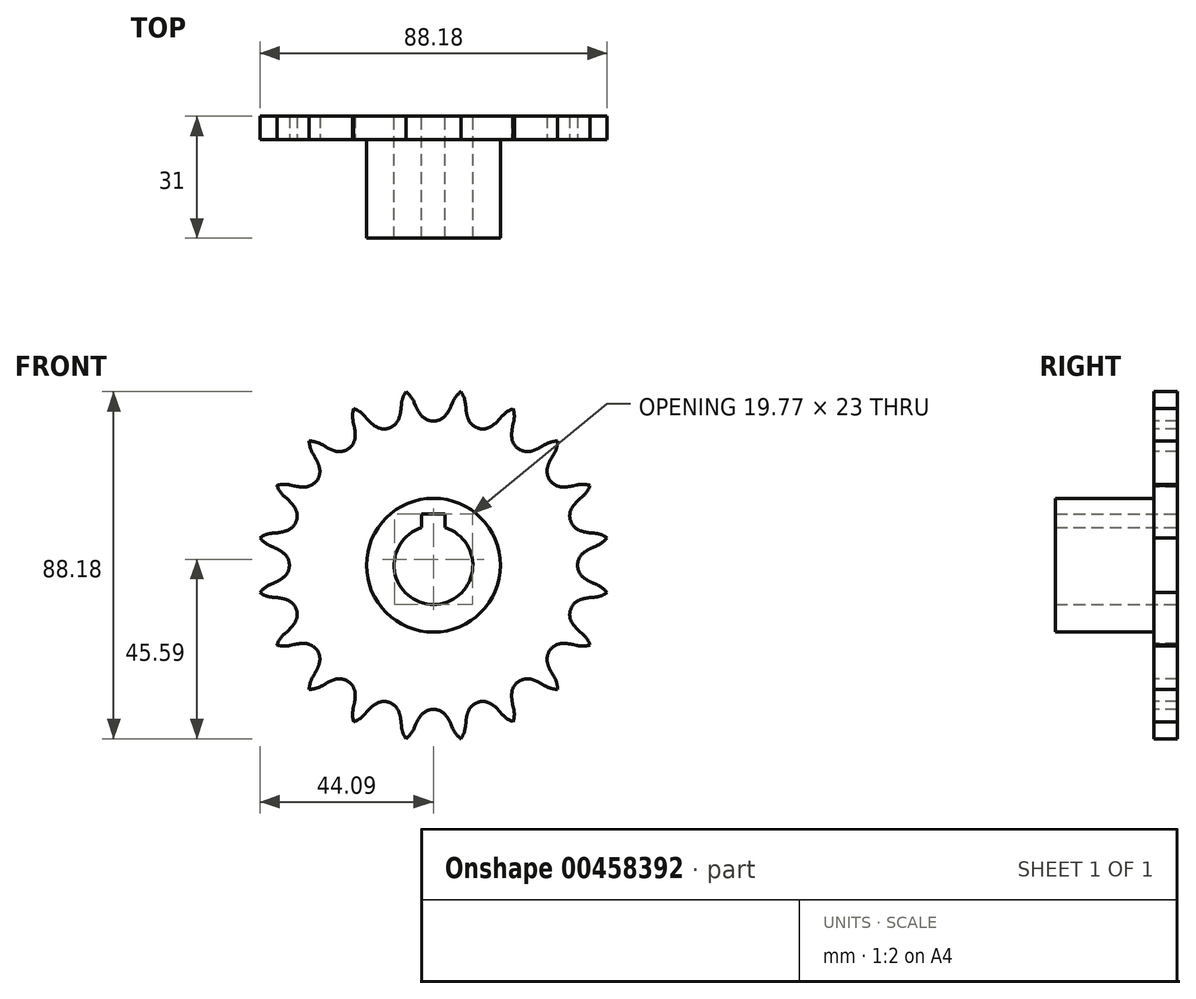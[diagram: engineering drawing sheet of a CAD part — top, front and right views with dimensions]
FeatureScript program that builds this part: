
annotation { "Feature Type Name" : "Feature", "Feature Type Description" : "" }
export const myFeature = defineFeature(function(context is Context, id is Id, definition is map)
    precondition{}
    {
        {
            var Q0;
            Q0=qCreatedBy(makeId("Front.planeOp"),FACE);
            var sketch = newSketch(context, id + "F0", { "sketchPlane" : qUnion([Q0])});
            skCircle(sketch, "E0", {"center": v(0, 0) * mm, "radius": 40.6 * mm, "construction": true});
            skLineSegment(sketch, "E1", {"start": v(0, 40.6) * mm, "end": v(5, 44.5) * mm, "construction": true});
            skLineSegment(sketch, "E2", {"start": v(-4.52, 40.5) * mm, "end": v(-4.9, 41.4) * mm});
            skLineSegment(sketch, "E3", {"start": v(0, 40.6) * mm, "end": v(17.06, 40.6) * mm, "construction": true});
            skArc(sketch, "E4", {"start": v(-4.52, 40.5) * mm, "mid": v(-3.9, 39.27) * mm, "end": v(-3.14, 38.14) * mm});
            skArc(sketch, "E5", {"start": v(-4.9, 41.4) * mm, "mid": v(-5.76, 42.88) * mm, "end": v(-6.98, 44.09) * mm});
            skLineSegment(sketch, "E6", {"start": v(0, 0) * mm, "end": v(-7.77, 49.08) * mm, "construction": true});
            skArc(sketch, "E7.trimOffspring", {"start": v(-3.14, 38.14) * mm, "mid": v(-1.75, 37.01) * mm, "end": v(0, 36.61) * mm});
            skArc(sketch, "E8.trimOffspring", {"start": v(13.29, 38.36) * mm, "mid": v(13.99, 39.43) * mm, "end": v(14.54, 40.6) * mm});
            skLineSegment(sketch, "E9", {"start": v(0, 40.6) * mm, "end": v(0, 0) * mm, "construction": true});
            skArc(sketch, "E10.MirrorCS", {"start": v(4.9, 41.4) * mm, "mid": v(5.76, 42.88) * mm, "end": v(6.98, 44.09) * mm});
            skLineSegment(sketch, "E11.MirrorCS", {"start": v(4.52, 40.5) * mm, "end": v(4.9, 41.4) * mm});
            skArc(sketch, "E12.MirrorCS", {"start": v(4.52, 40.5) * mm, "mid": v(3.9, 39.27) * mm, "end": v(3.14, 38.14) * mm});
            skArc(sketch, "E13.MirrorCS", {"start": v(3.14, 38.14) * mm, "mid": v(1.75, 37.01) * mm, "end": v(0, 36.61) * mm});
            skArc(sketch, "E14.1.0", {"start": v(-17.45, 37.86) * mm, "mid": v(-18.73, 39) * mm, "end": v(-20.26, 39.77) * mm});
            skArc(sketch, "E14.1.1", {"start": v(-16.81, 37.12) * mm, "mid": v(-15.85, 36.14) * mm, "end": v(-14.77, 35.3) * mm});
            skLineSegment(sketch, "E14.1.2", {"start": v(-16.81, 37.12) * mm, "end": v(-17.45, 37.86) * mm});
            skArc(sketch, "E14.1.3", {"start": v(-14.77, 35.3) * mm, "mid": v(-13.1, 34.66) * mm, "end": v(-11.31, 34.82) * mm});
            skArc(sketch, "E14.1.4", {"start": v(-8.8, 37.24) * mm, "mid": v(-9.78, 35.74) * mm, "end": v(-11.31, 34.82) * mm});
            skArc(sketch, "E14.1.5", {"start": v(-8.22, 39.9) * mm, "mid": v(-8.42, 38.56) * mm, "end": v(-8.8, 37.24) * mm});
            skLineSegment(sketch, "E14.1.6", {"start": v(-8.22, 39.9) * mm, "end": v(-8.13, 40.89) * mm});
            skArc(sketch, "E14.1.7", {"start": v(-8.13, 40.89) * mm, "mid": v(-7.77, 42.56) * mm, "end": v(-6.98, 44.09) * mm});
            skArc(sketch, "E14.2.0", {"start": v(-28.3, 30.61) * mm, "mid": v(-29.87, 31.3) * mm, "end": v(-31.56, 31.56) * mm});
            skArc(sketch, "E14.2.1", {"start": v(-27.46, 30.1) * mm, "mid": v(-26.24, 29.48) * mm, "end": v(-24.96, 29.01) * mm});
            skLineSegment(sketch, "E14.2.2", {"start": v(-27.46, 30.1) * mm, "end": v(-28.3, 30.61) * mm});
            skArc(sketch, "E14.2.3", {"start": v(-24.96, 29.01) * mm, "mid": v(-23.17, 28.92) * mm, "end": v(-21.52, 29.62) * mm});
            skArc(sketch, "E14.2.4", {"start": v(-19.88, 32.7) * mm, "mid": v(-20.34, 30.97) * mm, "end": v(-21.52, 29.62) * mm});
            skArc(sketch, "E14.2.5", {"start": v(-20.15, 35.42) * mm, "mid": v(-19.92, 34.07) * mm, "end": v(-19.88, 32.7) * mm});
            skLineSegment(sketch, "E14.2.6", {"start": v(-20.15, 35.42) * mm, "end": v(-20.37, 36.37) * mm});
            skArc(sketch, "E14.2.7", {"start": v(-20.37, 36.37) * mm, "mid": v(-20.54, 38.08) * mm, "end": v(-20.26, 39.77) * mm});
            skArc(sketch, "E14.3.0", {"start": v(-36.37, 20.37) * mm, "mid": v(-38.08, 20.54) * mm, "end": v(-39.77, 20.26) * mm});
            skArc(sketch, "E14.3.1", {"start": v(-35.42, 20.15) * mm, "mid": v(-34.07, 19.92) * mm, "end": v(-32.7, 19.88) * mm});
            skLineSegment(sketch, "E14.3.2", {"start": v(-35.42, 20.15) * mm, "end": v(-36.37, 20.37) * mm});
            skArc(sketch, "E14.3.3", {"start": v(-32.7, 19.88) * mm, "mid": v(-30.97, 20.34) * mm, "end": v(-29.62, 21.52) * mm});
            skArc(sketch, "E14.3.4", {"start": v(-29.01, 24.96) * mm, "mid": v(-28.92, 23.17) * mm, "end": v(-29.62, 21.52) * mm});
            skArc(sketch, "E14.3.5", {"start": v(-30.1, 27.46) * mm, "mid": v(-29.48, 26.24) * mm, "end": v(-29.01, 24.96) * mm});
            skLineSegment(sketch, "E14.3.6", {"start": v(-30.1, 27.46) * mm, "end": v(-30.61, 28.3) * mm});
            skArc(sketch, "E14.3.7", {"start": v(-30.61, 28.3) * mm, "mid": v(-31.3, 29.87) * mm, "end": v(-31.56, 31.56) * mm});
            skArc(sketch, "E14.4.0", {"start": v(-40.89, 8.13) * mm, "mid": v(-42.56, 7.77) * mm, "end": v(-44.09, 6.98) * mm});
            skArc(sketch, "E14.4.1", {"start": v(-39.9, 8.22) * mm, "mid": v(-38.56, 8.42) * mm, "end": v(-37.24, 8.8) * mm});
            skLineSegment(sketch, "E14.4.2", {"start": v(-39.9, 8.22) * mm, "end": v(-40.89, 8.13) * mm});
            skArc(sketch, "E14.4.3", {"start": v(-37.24, 8.8) * mm, "mid": v(-35.74, 9.78) * mm, "end": v(-34.82, 11.31) * mm});
            skArc(sketch, "E14.4.4", {"start": v(-35.3, 14.77) * mm, "mid": v(-34.66, 13.1) * mm, "end": v(-34.82, 11.31) * mm});
            skArc(sketch, "E14.4.5", {"start": v(-37.12, 16.81) * mm, "mid": v(-36.14, 15.85) * mm, "end": v(-35.3, 14.77) * mm});
            skLineSegment(sketch, "E14.4.6", {"start": v(-37.12, 16.81) * mm, "end": v(-37.86, 17.45) * mm});
            skArc(sketch, "E14.4.7", {"start": v(-37.86, 17.45) * mm, "mid": v(-39, 18.73) * mm, "end": v(-39.77, 20.26) * mm});
            skArc(sketch, "E14.5.0", {"start": v(-41.4, -4.9) * mm, "mid": v(-42.88, -5.76) * mm, "end": v(-44.09, -6.98) * mm});
            skArc(sketch, "E14.5.1", {"start": v(-40.5, -4.52) * mm, "mid": v(-39.27, -3.9) * mm, "end": v(-38.14, -3.14) * mm});
            skLineSegment(sketch, "E14.5.2", {"start": v(-40.5, -4.52) * mm, "end": v(-41.4, -4.9) * mm});
            skArc(sketch, "E14.5.3", {"start": v(-38.14, -3.14) * mm, "mid": v(-37.01, -1.75) * mm, "end": v(-36.61, 0) * mm});
            skArc(sketch, "E14.5.4", {"start": v(-38.14, 3.14) * mm, "mid": v(-37.01, 1.75) * mm, "end": v(-36.61, 0) * mm});
            skArc(sketch, "E14.5.5", {"start": v(-40.5, 4.52) * mm, "mid": v(-39.27, 3.9) * mm, "end": v(-38.14, 3.14) * mm});
            skLineSegment(sketch, "E14.5.6", {"start": v(-40.5, 4.52) * mm, "end": v(-41.4, 4.9) * mm});
            skArc(sketch, "E14.5.7", {"start": v(-41.4, 4.9) * mm, "mid": v(-42.88, 5.76) * mm, "end": v(-44.09, 6.98) * mm});
            skArc(sketch, "E14.6.0", {"start": v(-37.86, -17.45) * mm, "mid": v(-39, -18.73) * mm, "end": v(-39.77, -20.26) * mm});
            skArc(sketch, "E14.6.1", {"start": v(-37.12, -16.81) * mm, "mid": v(-36.14, -15.85) * mm, "end": v(-35.3, -14.77) * mm});
            skLineSegment(sketch, "E14.6.2", {"start": v(-37.12, -16.81) * mm, "end": v(-37.86, -17.45) * mm});
            skArc(sketch, "E14.6.3", {"start": v(-35.3, -14.77) * mm, "mid": v(-34.66, -13.1) * mm, "end": v(-34.82, -11.31) * mm});
            skArc(sketch, "E14.6.4", {"start": v(-37.24, -8.8) * mm, "mid": v(-35.74, -9.78) * mm, "end": v(-34.82, -11.31) * mm});
            skArc(sketch, "E14.6.5", {"start": v(-39.9, -8.22) * mm, "mid": v(-38.56, -8.42) * mm, "end": v(-37.24, -8.8) * mm});
            skLineSegment(sketch, "E14.6.6", {"start": v(-39.9, -8.22) * mm, "end": v(-40.89, -8.13) * mm});
            skArc(sketch, "E14.6.7", {"start": v(-40.89, -8.13) * mm, "mid": v(-42.56, -7.77) * mm, "end": v(-44.09, -6.98) * mm});
            skArc(sketch, "E14.7.0", {"start": v(-30.61, -28.3) * mm, "mid": v(-31.3, -29.87) * mm, "end": v(-31.56, -31.56) * mm});
            skArc(sketch, "E14.7.1", {"start": v(-30.1, -27.46) * mm, "mid": v(-29.48, -26.24) * mm, "end": v(-29.01, -24.96) * mm});
            skLineSegment(sketch, "E14.7.2", {"start": v(-30.1, -27.46) * mm, "end": v(-30.61, -28.3) * mm});
            skArc(sketch, "E14.7.3", {"start": v(-29.01, -24.96) * mm, "mid": v(-28.92, -23.17) * mm, "end": v(-29.62, -21.52) * mm});
            skArc(sketch, "E14.7.4", {"start": v(-32.7, -19.88) * mm, "mid": v(-30.97, -20.34) * mm, "end": v(-29.62, -21.52) * mm});
            skArc(sketch, "E14.7.5", {"start": v(-35.42, -20.15) * mm, "mid": v(-34.07, -19.92) * mm, "end": v(-32.7, -19.88) * mm});
            skLineSegment(sketch, "E14.7.6", {"start": v(-35.42, -20.15) * mm, "end": v(-36.37, -20.37) * mm});
            skArc(sketch, "E14.7.7", {"start": v(-36.37, -20.37) * mm, "mid": v(-38.08, -20.54) * mm, "end": v(-39.77, -20.26) * mm});
            skArc(sketch, "E14.8.0", {"start": v(-20.37, -36.37) * mm, "mid": v(-20.54, -38.08) * mm, "end": v(-20.26, -39.77) * mm});
            skArc(sketch, "E14.8.1", {"start": v(-20.15, -35.42) * mm, "mid": v(-19.92, -34.07) * mm, "end": v(-19.88, -32.7) * mm});
            skLineSegment(sketch, "E14.8.2", {"start": v(-20.15, -35.42) * mm, "end": v(-20.37, -36.37) * mm});
            skArc(sketch, "E14.8.3", {"start": v(-19.88, -32.7) * mm, "mid": v(-20.34, -30.97) * mm, "end": v(-21.52, -29.62) * mm});
            skArc(sketch, "E14.8.4", {"start": v(-24.96, -29.01) * mm, "mid": v(-23.17, -28.92) * mm, "end": v(-21.52, -29.62) * mm});
            skArc(sketch, "E14.8.5", {"start": v(-27.46, -30.1) * mm, "mid": v(-26.24, -29.48) * mm, "end": v(-24.96, -29.01) * mm});
            skLineSegment(sketch, "E14.8.6", {"start": v(-27.46, -30.1) * mm, "end": v(-28.3, -30.61) * mm});
            skArc(sketch, "E14.8.7", {"start": v(-28.3, -30.61) * mm, "mid": v(-29.87, -31.3) * mm, "end": v(-31.56, -31.56) * mm});
            skArc(sketch, "E14.9.0", {"start": v(-8.13, -40.89) * mm, "mid": v(-7.77, -42.56) * mm, "end": v(-6.98, -44.09) * mm});
            skArc(sketch, "E14.9.1", {"start": v(-8.22, -39.9) * mm, "mid": v(-8.42, -38.56) * mm, "end": v(-8.8, -37.24) * mm});
            skLineSegment(sketch, "E14.9.2", {"start": v(-8.22, -39.9) * mm, "end": v(-8.13, -40.89) * mm});
            skArc(sketch, "E14.9.3", {"start": v(-8.8, -37.24) * mm, "mid": v(-9.78, -35.74) * mm, "end": v(-11.31, -34.82) * mm});
            skArc(sketch, "E14.9.4", {"start": v(-14.77, -35.3) * mm, "mid": v(-13.1, -34.66) * mm, "end": v(-11.31, -34.82) * mm});
            skArc(sketch, "E14.9.5", {"start": v(-16.81, -37.12) * mm, "mid": v(-15.85, -36.14) * mm, "end": v(-14.77, -35.3) * mm});
            skLineSegment(sketch, "E14.9.6", {"start": v(-16.81, -37.12) * mm, "end": v(-17.45, -37.86) * mm});
            skArc(sketch, "E14.9.7", {"start": v(-17.45, -37.86) * mm, "mid": v(-18.73, -39) * mm, "end": v(-20.26, -39.77) * mm});
            skArc(sketch, "E14.10.0", {"start": v(4.9, -41.4) * mm, "mid": v(5.76, -42.88) * mm, "end": v(6.98, -44.09) * mm});
            skArc(sketch, "E14.10.1", {"start": v(4.52, -40.5) * mm, "mid": v(3.9, -39.27) * mm, "end": v(3.14, -38.14) * mm});
            skLineSegment(sketch, "E14.10.2", {"start": v(4.52, -40.5) * mm, "end": v(4.9, -41.4) * mm});
            skArc(sketch, "E14.10.3", {"start": v(3.14, -38.14) * mm, "mid": v(1.75, -37.01) * mm, "end": v(0, -36.61) * mm});
            skArc(sketch, "E14.10.4", {"start": v(-3.14, -38.14) * mm, "mid": v(-1.75, -37.01) * mm, "end": v(0, -36.61) * mm});
            skArc(sketch, "E14.10.5", {"start": v(-4.52, -40.5) * mm, "mid": v(-3.9, -39.27) * mm, "end": v(-3.14, -38.14) * mm});
            skLineSegment(sketch, "E14.10.6", {"start": v(-4.52, -40.5) * mm, "end": v(-4.9, -41.4) * mm});
            skArc(sketch, "E14.10.7", {"start": v(-4.9, -41.4) * mm, "mid": v(-5.76, -42.88) * mm, "end": v(-6.98, -44.09) * mm});
            skArc(sketch, "E14.11.0", {"start": v(17.45, -37.86) * mm, "mid": v(18.73, -39) * mm, "end": v(20.26, -39.77) * mm});
            skArc(sketch, "E14.11.1", {"start": v(16.81, -37.12) * mm, "mid": v(15.85, -36.14) * mm, "end": v(14.77, -35.3) * mm});
            skLineSegment(sketch, "E14.11.2", {"start": v(16.81, -37.12) * mm, "end": v(17.45, -37.86) * mm});
            skArc(sketch, "E14.11.3", {"start": v(14.77, -35.3) * mm, "mid": v(13.1, -34.66) * mm, "end": v(11.31, -34.82) * mm});
            skArc(sketch, "E14.11.4", {"start": v(8.8, -37.24) * mm, "mid": v(9.78, -35.74) * mm, "end": v(11.31, -34.82) * mm});
            skArc(sketch, "E14.11.5", {"start": v(8.22, -39.9) * mm, "mid": v(8.42, -38.56) * mm, "end": v(8.8, -37.24) * mm});
            skLineSegment(sketch, "E14.11.6", {"start": v(8.22, -39.9) * mm, "end": v(8.13, -40.89) * mm});
            skArc(sketch, "E14.11.7", {"start": v(8.13, -40.89) * mm, "mid": v(7.77, -42.56) * mm, "end": v(6.98, -44.09) * mm});
            skArc(sketch, "E14.12.0", {"start": v(28.3, -30.61) * mm, "mid": v(29.87, -31.3) * mm, "end": v(31.56, -31.56) * mm});
            skArc(sketch, "E14.12.1", {"start": v(27.46, -30.1) * mm, "mid": v(26.24, -29.48) * mm, "end": v(24.96, -29.01) * mm});
            skLineSegment(sketch, "E14.12.2", {"start": v(27.46, -30.1) * mm, "end": v(28.3, -30.61) * mm});
            skArc(sketch, "E14.12.3", {"start": v(24.96, -29.01) * mm, "mid": v(23.17, -28.92) * mm, "end": v(21.52, -29.62) * mm});
            skArc(sketch, "E14.12.4", {"start": v(19.88, -32.7) * mm, "mid": v(20.34, -30.97) * mm, "end": v(21.52, -29.62) * mm});
            skArc(sketch, "E14.12.5", {"start": v(20.15, -35.42) * mm, "mid": v(19.92, -34.07) * mm, "end": v(19.88, -32.7) * mm});
            skLineSegment(sketch, "E14.12.6", {"start": v(20.15, -35.42) * mm, "end": v(20.37, -36.37) * mm});
            skArc(sketch, "E14.12.7", {"start": v(20.37, -36.37) * mm, "mid": v(20.54, -38.08) * mm, "end": v(20.26, -39.77) * mm});
            skArc(sketch, "E14.13.0", {"start": v(36.37, -20.37) * mm, "mid": v(38.08, -20.54) * mm, "end": v(39.77, -20.26) * mm});
            skArc(sketch, "E14.13.1", {"start": v(35.42, -20.15) * mm, "mid": v(34.07, -19.92) * mm, "end": v(32.7, -19.88) * mm});
            skLineSegment(sketch, "E14.13.2", {"start": v(35.42, -20.15) * mm, "end": v(36.37, -20.37) * mm});
            skArc(sketch, "E14.13.3", {"start": v(32.7, -19.88) * mm, "mid": v(30.97, -20.34) * mm, "end": v(29.62, -21.52) * mm});
            skArc(sketch, "E14.13.4", {"start": v(29.01, -24.96) * mm, "mid": v(28.92, -23.17) * mm, "end": v(29.62, -21.52) * mm});
            skArc(sketch, "E14.13.5", {"start": v(30.1, -27.46) * mm, "mid": v(29.48, -26.24) * mm, "end": v(29.01, -24.96) * mm});
            skLineSegment(sketch, "E14.13.6", {"start": v(30.1, -27.46) * mm, "end": v(30.61, -28.3) * mm});
            skArc(sketch, "E14.13.7", {"start": v(30.61, -28.3) * mm, "mid": v(31.3, -29.87) * mm, "end": v(31.56, -31.56) * mm});
            skArc(sketch, "E14.14.0", {"start": v(40.89, -8.13) * mm, "mid": v(42.56, -7.77) * mm, "end": v(44.09, -6.98) * mm});
            skArc(sketch, "E14.14.1", {"start": v(39.9, -8.22) * mm, "mid": v(38.56, -8.42) * mm, "end": v(37.24, -8.8) * mm});
            skLineSegment(sketch, "E14.14.2", {"start": v(39.9, -8.22) * mm, "end": v(40.89, -8.13) * mm});
            skArc(sketch, "E14.14.3", {"start": v(37.24, -8.8) * mm, "mid": v(35.74, -9.78) * mm, "end": v(34.82, -11.31) * mm});
            skArc(sketch, "E14.14.4", {"start": v(35.3, -14.77) * mm, "mid": v(34.66, -13.1) * mm, "end": v(34.82, -11.31) * mm});
            skArc(sketch, "E14.14.5", {"start": v(37.12, -16.81) * mm, "mid": v(36.14, -15.85) * mm, "end": v(35.3, -14.77) * mm});
            skLineSegment(sketch, "E14.14.6", {"start": v(37.12, -16.81) * mm, "end": v(37.86, -17.45) * mm});
            skArc(sketch, "E14.14.7", {"start": v(37.86, -17.45) * mm, "mid": v(39, -18.73) * mm, "end": v(39.77, -20.26) * mm});
            skArc(sketch, "E14.15.0", {"start": v(41.4, 4.9) * mm, "mid": v(42.88, 5.76) * mm, "end": v(44.09, 6.98) * mm});
            skArc(sketch, "E14.15.1", {"start": v(40.5, 4.52) * mm, "mid": v(39.27, 3.9) * mm, "end": v(38.14, 3.14) * mm});
            skLineSegment(sketch, "E14.15.2", {"start": v(40.5, 4.52) * mm, "end": v(41.4, 4.9) * mm});
            skArc(sketch, "E14.15.3", {"start": v(38.14, 3.14) * mm, "mid": v(37.01, 1.75) * mm, "end": v(36.61, 0) * mm});
            skArc(sketch, "E14.15.4", {"start": v(38.14, -3.14) * mm, "mid": v(37.01, -1.75) * mm, "end": v(36.61, 0) * mm});
            skArc(sketch, "E14.15.5", {"start": v(40.5, -4.52) * mm, "mid": v(39.27, -3.9) * mm, "end": v(38.14, -3.14) * mm});
            skLineSegment(sketch, "E14.15.6", {"start": v(40.5, -4.52) * mm, "end": v(41.4, -4.9) * mm});
            skArc(sketch, "E14.15.7", {"start": v(41.4, -4.9) * mm, "mid": v(42.88, -5.76) * mm, "end": v(44.09, -6.98) * mm});
            skArc(sketch, "E14.16.0", {"start": v(37.86, 17.45) * mm, "mid": v(39, 18.73) * mm, "end": v(39.77, 20.26) * mm});
            skArc(sketch, "E14.16.1", {"start": v(37.12, 16.81) * mm, "mid": v(36.14, 15.85) * mm, "end": v(35.3, 14.77) * mm});
            skLineSegment(sketch, "E14.16.2", {"start": v(37.12, 16.81) * mm, "end": v(37.86, 17.45) * mm});
            skArc(sketch, "E14.16.3", {"start": v(35.3, 14.77) * mm, "mid": v(34.66, 13.1) * mm, "end": v(34.82, 11.31) * mm});
            skArc(sketch, "E14.16.4", {"start": v(37.24, 8.8) * mm, "mid": v(35.74, 9.78) * mm, "end": v(34.82, 11.31) * mm});
            skArc(sketch, "E14.16.5", {"start": v(39.9, 8.22) * mm, "mid": v(38.56, 8.42) * mm, "end": v(37.24, 8.8) * mm});
            skLineSegment(sketch, "E14.16.6", {"start": v(39.9, 8.22) * mm, "end": v(40.89, 8.13) * mm});
            skArc(sketch, "E14.16.7", {"start": v(40.89, 8.13) * mm, "mid": v(42.56, 7.77) * mm, "end": v(44.09, 6.98) * mm});
            skArc(sketch, "E14.17.0", {"start": v(30.61, 28.3) * mm, "mid": v(31.3, 29.87) * mm, "end": v(31.56, 31.56) * mm});
            skArc(sketch, "E14.17.1", {"start": v(30.1, 27.46) * mm, "mid": v(29.48, 26.24) * mm, "end": v(29.01, 24.96) * mm});
            skLineSegment(sketch, "E14.17.2", {"start": v(30.1, 27.46) * mm, "end": v(30.61, 28.3) * mm});
            skArc(sketch, "E14.17.3", {"start": v(29.01, 24.96) * mm, "mid": v(28.92, 23.17) * mm, "end": v(29.62, 21.52) * mm});
            skArc(sketch, "E14.17.4", {"start": v(32.7, 19.88) * mm, "mid": v(30.97, 20.34) * mm, "end": v(29.62, 21.52) * mm});
            skArc(sketch, "E14.17.5", {"start": v(35.42, 20.15) * mm, "mid": v(34.07, 19.92) * mm, "end": v(32.7, 19.88) * mm});
            skLineSegment(sketch, "E14.17.6", {"start": v(35.42, 20.15) * mm, "end": v(36.37, 20.37) * mm});
            skArc(sketch, "E14.17.7", {"start": v(36.37, 20.37) * mm, "mid": v(38.08, 20.54) * mm, "end": v(39.77, 20.26) * mm});
            skArc(sketch, "E14.18.0", {"start": v(20.37, 36.37) * mm, "mid": v(20.54, 38.08) * mm, "end": v(20.26, 39.77) * mm});
            skArc(sketch, "E14.18.1", {"start": v(20.15, 35.42) * mm, "mid": v(19.92, 34.07) * mm, "end": v(19.88, 32.7) * mm});
            skLineSegment(sketch, "E14.18.2", {"start": v(20.15, 35.42) * mm, "end": v(20.37, 36.37) * mm});
            skArc(sketch, "E14.18.3", {"start": v(19.88, 32.7) * mm, "mid": v(20.34, 30.97) * mm, "end": v(21.52, 29.62) * mm});
            skArc(sketch, "E14.18.4", {"start": v(24.96, 29.01) * mm, "mid": v(23.17, 28.92) * mm, "end": v(21.52, 29.62) * mm});
            skArc(sketch, "E14.18.5", {"start": v(27.46, 30.1) * mm, "mid": v(26.24, 29.48) * mm, "end": v(24.96, 29.01) * mm});
            skLineSegment(sketch, "E14.18.6", {"start": v(27.46, 30.1) * mm, "end": v(28.3, 30.61) * mm});
            skArc(sketch, "E14.18.7", {"start": v(28.3, 30.61) * mm, "mid": v(29.87, 31.3) * mm, "end": v(31.56, 31.56) * mm});
            skArc(sketch, "E14.19.0", {"start": v(8.13, 40.89) * mm, "mid": v(7.77, 42.56) * mm, "end": v(6.98, 44.09) * mm});
            skArc(sketch, "E14.19.1", {"start": v(8.22, 39.9) * mm, "mid": v(8.42, 38.56) * mm, "end": v(8.8, 37.24) * mm});
            skLineSegment(sketch, "E14.19.2", {"start": v(8.22, 39.9) * mm, "end": v(8.13, 40.89) * mm});
            skArc(sketch, "E14.19.3", {"start": v(8.8, 37.24) * mm, "mid": v(9.78, 35.74) * mm, "end": v(11.31, 34.82) * mm});
            skArc(sketch, "E14.19.4", {"start": v(14.77, 35.3) * mm, "mid": v(13.1, 34.66) * mm, "end": v(11.31, 34.82) * mm});
            skArc(sketch, "E14.19.5", {"start": v(16.81, 37.12) * mm, "mid": v(15.85, 36.14) * mm, "end": v(14.77, 35.3) * mm});
            skLineSegment(sketch, "E14.19.6", {"start": v(16.81, 37.12) * mm, "end": v(17.45, 37.86) * mm});
            skArc(sketch, "E14.19.7", {"start": v(17.45, 37.86) * mm, "mid": v(18.73, 39) * mm, "end": v(20.26, 39.77) * mm});
            skSolve(sketch);
        }
        {
            var Q0;
            Q0=makeQuery(id+"F0.imprint","IMPRINT",FACE,{"disambiguationData":[TD([[makeQuery(id+"F0.imprint","IMPRINT",EDGE,{"derivedFrom":sQuery(id+"F0.wireOp",EDGE,"E2")}),1.0]])]});
            extrude(context, id + "F1", {"entities" : qUnion([Q0]), "oppositeDirection" : true, "depth" : 6 * mm});
        }
        {
            var Q0;
            Q0=qCreatedBy(makeId("Front.planeOp"),FACE);
            var sketch = newSketch(context, id + "F2", { "sketchPlane" : qUnion([Q0])});
            skCircle(sketch, "E15", {"center": v(0, 0) * mm, "radius": 17 * mm});
            skCircle(sketch, "E16", {"center": v(0, 0) * mm, "radius": 10 * mm});
            skLineSegment(sketch, "E17.bottom", {"start": v(-3, 13) * mm, "end": v(3, 13) * mm});
            skLineSegment(sketch, "E17.top", {"start": v(-3, 7) * mm, "end": v(3, 7) * mm});
            skLineSegment(sketch, "E17.left", {"start": v(-3, 13) * mm, "end": v(-3, 7) * mm});
            skLineSegment(sketch, "E17.right", {"start": v(3, 13) * mm, "end": v(3, 7) * mm});
            skSolve(sketch);
        }
        {
            var Q0;
            Q0=makeQuery(id+"F2.imprint","IMPRINT",FACE,{"disambiguationData":[TD([[makeQuery(id+"F2.imprint","IMPRINT",EDGE,{"derivedFrom":sQuery(id+"F2.wireOp",EDGE,"E15")}),1.0]])]});
            extrude(context, id + "F3", {"entities" : qUnion([Q0]), "operationType" : NewBodyOperationType.ADD, "depth" : 25 * mm, "offsetDistance" : 25 * mm});
        }
        {
            var Q0;
            Q0=makeQuery(id+"F3.boolean.opBoolean","SPLIT",FACE,{"disambiguationData":[TD([makeQuery(id+"F3.opExtrude","SWEPT_FACE",FACE,{"disambiguationData":[OSD([sQuery(id+"F2.wireOp",EDGE,"E16")])]})])],"derivedFrom":makeQuery(id+"F1.opExtrude","CAP_FACE",FACE,{"disambiguationData":[OSD([sQuery(id+"F0.wireOp",EDGE,"E2"),sQuery(id+"F0.wireOp",EDGE,"E4"),sQuery(id+"F0.wireOp",EDGE,"E5"),sQuery(id+"F0.wireOp",EDGE,"E7.trimOffspring"),sQuery(id+"F0.wireOp",EDGE,"E10.MirrorCS"),sQuery(id+"F0.wireOp",EDGE,"E11.MirrorCS"),sQuery(id+"F0.wireOp",EDGE,"E12.MirrorCS"),sQuery(id+"F0.wireOp",EDGE,"E13.MirrorCS"),sQuery(id+"F0.wireOp",EDGE,"E14.1.0"),sQuery(id+"F0.wireOp",EDGE,"E14.1.1"),sQuery(id+"F0.wireOp",EDGE,"E14.1.2"),sQuery(id+"F0.wireOp",EDGE,"E14.1.3"),sQuery(id+"F0.wireOp",EDGE,"E14.1.4"),sQuery(id+"F0.wireOp",EDGE,"E14.1.5"),sQuery(id+"F0.wireOp",EDGE,"E14.1.6"),sQuery(id+"F0.wireOp",EDGE,"E14.1.7"),sQuery(id+"F0.wireOp",EDGE,"E14.2.0"),sQuery(id+"F0.wireOp",EDGE,"E14.2.1"),sQuery(id+"F0.wireOp",EDGE,"E14.2.2"),sQuery(id+"F0.wireOp",EDGE,"E14.2.3"),sQuery(id+"F0.wireOp",EDGE,"E14.2.4"),sQuery(id+"F0.wireOp",EDGE,"E14.2.5"),sQuery(id+"F0.wireOp",EDGE,"E14.2.6"),sQuery(id+"F0.wireOp",EDGE,"E14.2.7"),sQuery(id+"F0.wireOp",EDGE,"E14.3.0"),sQuery(id+"F0.wireOp",EDGE,"E14.3.1"),sQuery(id+"F0.wireOp",EDGE,"E14.3.2"),sQuery(id+"F0.wireOp",EDGE,"E14.3.3"),sQuery(id+"F0.wireOp",EDGE,"E14.3.4"),sQuery(id+"F0.wireOp",EDGE,"E14.3.5"),sQuery(id+"F0.wireOp",EDGE,"E14.3.6"),sQuery(id+"F0.wireOp",EDGE,"E14.3.7"),sQuery(id+"F0.wireOp",EDGE,"E14.4.0"),sQuery(id+"F0.wireOp",EDGE,"E14.4.1"),sQuery(id+"F0.wireOp",EDGE,"E14.4.2"),sQuery(id+"F0.wireOp",EDGE,"E14.4.3"),sQuery(id+"F0.wireOp",EDGE,"E14.4.4"),sQuery(id+"F0.wireOp",EDGE,"E14.4.5"),sQuery(id+"F0.wireOp",EDGE,"E14.4.6"),sQuery(id+"F0.wireOp",EDGE,"E14.4.7"),sQuery(id+"F0.wireOp",EDGE,"E14.5.0"),sQuery(id+"F0.wireOp",EDGE,"E14.5.1"),sQuery(id+"F0.wireOp",EDGE,"E14.5.2"),sQuery(id+"F0.wireOp",EDGE,"E14.5.3"),sQuery(id+"F0.wireOp",EDGE,"E14.5.4"),sQuery(id+"F0.wireOp",EDGE,"E14.5.5"),sQuery(id+"F0.wireOp",EDGE,"E14.5.6"),sQuery(id+"F0.wireOp",EDGE,"E14.5.7"),sQuery(id+"F0.wireOp",EDGE,"E14.6.0"),sQuery(id+"F0.wireOp",EDGE,"E14.6.1"),sQuery(id+"F0.wireOp",EDGE,"E14.6.2"),sQuery(id+"F0.wireOp",EDGE,"E14.6.3"),sQuery(id+"F0.wireOp",EDGE,"E14.6.4"),sQuery(id+"F0.wireOp",EDGE,"E14.6.5"),sQuery(id+"F0.wireOp",EDGE,"E14.6.6"),sQuery(id+"F0.wireOp",EDGE,"E14.6.7"),sQuery(id+"F0.wireOp",EDGE,"E14.7.0"),sQuery(id+"F0.wireOp",EDGE,"E14.7.1"),sQuery(id+"F0.wireOp",EDGE,"E14.7.2"),sQuery(id+"F0.wireOp",EDGE,"E14.7.3"),sQuery(id+"F0.wireOp",EDGE,"E14.7.4"),sQuery(id+"F0.wireOp",EDGE,"E14.7.5"),sQuery(id+"F0.wireOp",EDGE,"E14.7.6"),sQuery(id+"F0.wireOp",EDGE,"E14.7.7"),sQuery(id+"F0.wireOp",EDGE,"E14.8.0"),sQuery(id+"F0.wireOp",EDGE,"E14.8.1"),sQuery(id+"F0.wireOp",EDGE,"E14.8.2"),sQuery(id+"F0.wireOp",EDGE,"E14.8.3"),sQuery(id+"F0.wireOp",EDGE,"E14.8.4"),sQuery(id+"F0.wireOp",EDGE,"E14.8.5"),sQuery(id+"F0.wireOp",EDGE,"E14.8.6"),sQuery(id+"F0.wireOp",EDGE,"E14.8.7"),sQuery(id+"F0.wireOp",EDGE,"E14.9.0"),sQuery(id+"F0.wireOp",EDGE,"E14.9.1"),sQuery(id+"F0.wireOp",EDGE,"E14.9.2"),sQuery(id+"F0.wireOp",EDGE,"E14.9.3"),sQuery(id+"F0.wireOp",EDGE,"E14.9.4"),sQuery(id+"F0.wireOp",EDGE,"E14.9.5"),sQuery(id+"F0.wireOp",EDGE,"E14.9.6"),sQuery(id+"F0.wireOp",EDGE,"E14.9.7"),sQuery(id+"F0.wireOp",EDGE,"E14.10.0"),sQuery(id+"F0.wireOp",EDGE,"E14.10.1"),sQuery(id+"F0.wireOp",EDGE,"E14.10.2"),sQuery(id+"F0.wireOp",EDGE,"E14.10.3"),sQuery(id+"F0.wireOp",EDGE,"E14.10.4"),sQuery(id+"F0.wireOp",EDGE,"E14.10.5"),sQuery(id+"F0.wireOp",EDGE,"E14.10.6"),sQuery(id+"F0.wireOp",EDGE,"E14.10.7"),sQuery(id+"F0.wireOp",EDGE,"E14.11.0"),sQuery(id+"F0.wireOp",EDGE,"E14.11.1"),sQuery(id+"F0.wireOp",EDGE,"E14.11.2"),sQuery(id+"F0.wireOp",EDGE,"E14.11.3"),sQuery(id+"F0.wireOp",EDGE,"E14.11.4"),sQuery(id+"F0.wireOp",EDGE,"E14.11.5"),sQuery(id+"F0.wireOp",EDGE,"E14.11.6"),sQuery(id+"F0.wireOp",EDGE,"E14.11.7"),sQuery(id+"F0.wireOp",EDGE,"E14.12.0"),sQuery(id+"F0.wireOp",EDGE,"E14.12.1"),sQuery(id+"F0.wireOp",EDGE,"E14.12.2"),sQuery(id+"F0.wireOp",EDGE,"E14.12.3"),sQuery(id+"F0.wireOp",EDGE,"E14.12.4"),sQuery(id+"F0.wireOp",EDGE,"E14.12.5"),sQuery(id+"F0.wireOp",EDGE,"E14.12.6"),sQuery(id+"F0.wireOp",EDGE,"E14.12.7"),sQuery(id+"F0.wireOp",EDGE,"E14.13.0"),sQuery(id+"F0.wireOp",EDGE,"E14.13.1"),sQuery(id+"F0.wireOp",EDGE,"E14.13.2"),sQuery(id+"F0.wireOp",EDGE,"E14.13.3"),sQuery(id+"F0.wireOp",EDGE,"E14.13.4"),sQuery(id+"F0.wireOp",EDGE,"E14.13.5"),sQuery(id+"F0.wireOp",EDGE,"E14.13.6"),sQuery(id+"F0.wireOp",EDGE,"E14.13.7"),sQuery(id+"F0.wireOp",EDGE,"E14.14.0"),sQuery(id+"F0.wireOp",EDGE,"E14.14.1"),sQuery(id+"F0.wireOp",EDGE,"E14.14.2"),sQuery(id+"F0.wireOp",EDGE,"E14.14.3"),sQuery(id+"F0.wireOp",EDGE,"E14.14.4"),sQuery(id+"F0.wireOp",EDGE,"E14.14.5"),sQuery(id+"F0.wireOp",EDGE,"E14.14.6"),sQuery(id+"F0.wireOp",EDGE,"E14.14.7"),sQuery(id+"F0.wireOp",EDGE,"E14.15.0"),sQuery(id+"F0.wireOp",EDGE,"E14.15.1"),sQuery(id+"F0.wireOp",EDGE,"E14.15.2"),sQuery(id+"F0.wireOp",EDGE,"E14.15.3"),sQuery(id+"F0.wireOp",EDGE,"E14.15.4"),sQuery(id+"F0.wireOp",EDGE,"E14.15.5"),sQuery(id+"F0.wireOp",EDGE,"E14.15.6"),sQuery(id+"F0.wireOp",EDGE,"E14.15.7"),sQuery(id+"F0.wireOp",EDGE,"E14.16.0"),sQuery(id+"F0.wireOp",EDGE,"E14.16.1"),sQuery(id+"F0.wireOp",EDGE,"E14.16.2"),sQuery(id+"F0.wireOp",EDGE,"E14.16.3"),sQuery(id+"F0.wireOp",EDGE,"E14.16.4"),sQuery(id+"F0.wireOp",EDGE,"E14.16.5"),sQuery(id+"F0.wireOp",EDGE,"E14.16.6"),sQuery(id+"F0.wireOp",EDGE,"E14.16.7"),sQuery(id+"F0.wireOp",EDGE,"E14.17.0"),sQuery(id+"F0.wireOp",EDGE,"E14.17.1"),sQuery(id+"F0.wireOp",EDGE,"E14.17.2"),sQuery(id+"F0.wireOp",EDGE,"E14.17.3"),sQuery(id+"F0.wireOp",EDGE,"E14.17.4"),sQuery(id+"F0.wireOp",EDGE,"E14.17.5"),sQuery(id+"F0.wireOp",EDGE,"E14.17.6"),sQuery(id+"F0.wireOp",EDGE,"E14.17.7"),sQuery(id+"F0.wireOp",EDGE,"E14.18.0"),sQuery(id+"F0.wireOp",EDGE,"E14.18.1"),sQuery(id+"F0.wireOp",EDGE,"E14.18.2"),sQuery(id+"F0.wireOp",EDGE,"E14.18.3"),sQuery(id+"F0.wireOp",EDGE,"E14.18.4"),sQuery(id+"F0.wireOp",EDGE,"E14.18.5"),sQuery(id+"F0.wireOp",EDGE,"E14.18.6"),sQuery(id+"F0.wireOp",EDGE,"E14.18.7"),sQuery(id+"F0.wireOp",EDGE,"E14.19.0"),sQuery(id+"F0.wireOp",EDGE,"E14.19.1"),sQuery(id+"F0.wireOp",EDGE,"E14.19.2"),sQuery(id+"F0.wireOp",EDGE,"E14.19.3"),sQuery(id+"F0.wireOp",EDGE,"E14.19.4"),sQuery(id+"F0.wireOp",EDGE,"E14.19.5"),sQuery(id+"F0.wireOp",EDGE,"E14.19.6"),sQuery(id+"F0.wireOp",EDGE,"E14.19.7")])],"isStart":true})});
            extrude(context, id + "F4", {"entities" : qUnion([Q0]), "operationType" : NewBodyOperationType.REMOVE, "oppositeDirection" : true, "depth" : 25 * mm});
        }
        {
            var Q0;
            Q0=qCreatedBy(makeId("Top.planeOp"),FACE);
            cPlane(context, id + "F5", {"entities" : qUnion([Q0]), "cplaneType" : CPlaneType.OFFSET, "offset" : 17 * mm, "width" : 150 * mm, "height" : 150 * mm});
        }
    });
